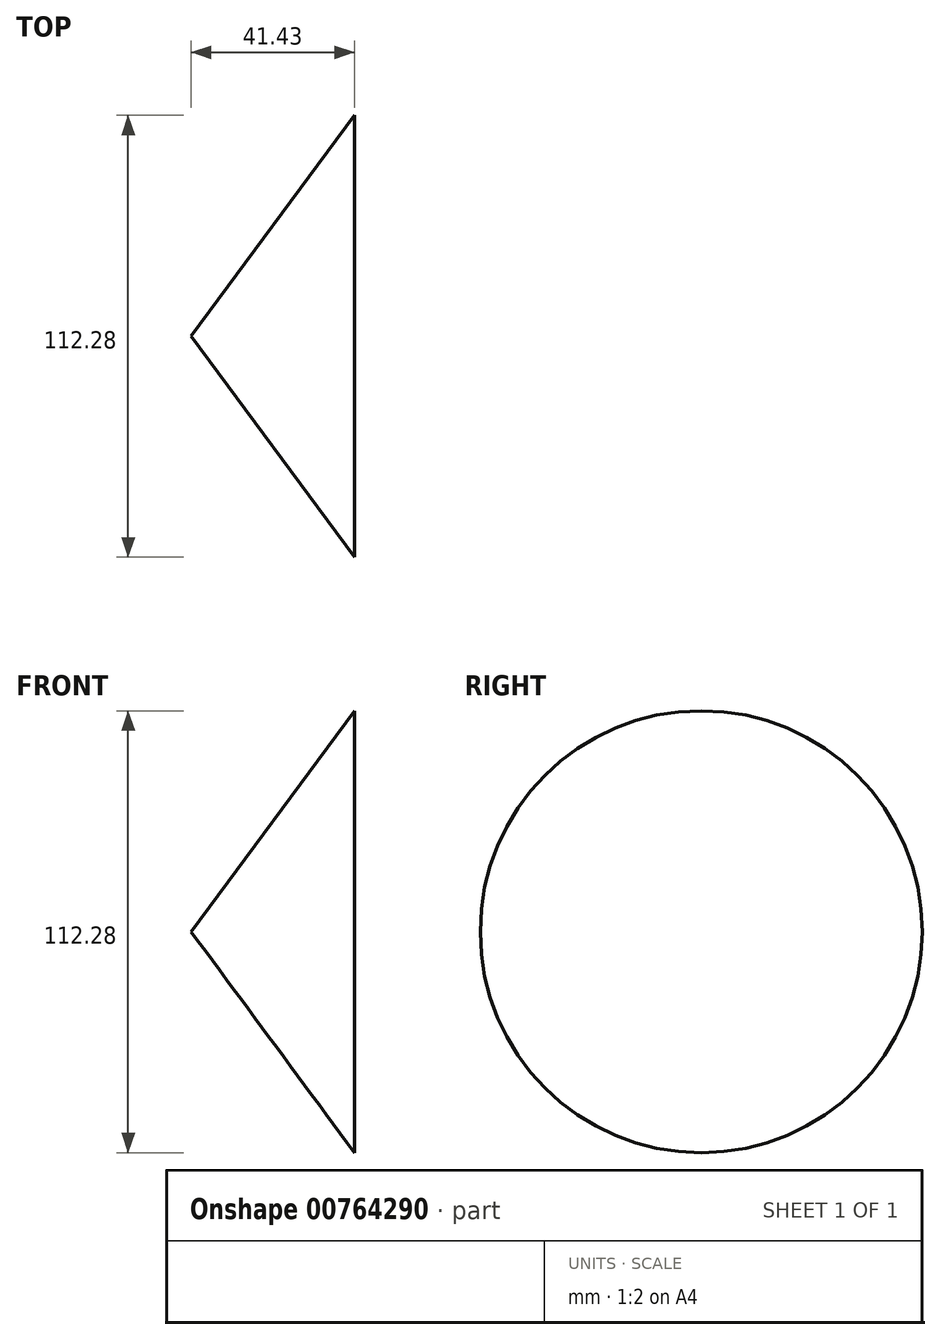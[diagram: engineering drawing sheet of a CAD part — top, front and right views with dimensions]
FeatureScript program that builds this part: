
annotation { "Feature Type Name" : "Feature", "Feature Type Description" : "" }
export const myFeature = defineFeature(function(context is Context, id is Id, definition is map)
    precondition{}
    {
        {
            var Q0;
            Q0=qCreatedBy(makeId("Front.planeOp"),FACE);
            var sketch = newSketch(context, id + "F0", { "sketchPlane" : qUnion([Q0])});
            skLineSegment(sketch, "E0", {"start": v(0, 56.14) * mm, "end": v(-41.43, 0) * mm});
            skLineSegment(sketch, "E1", {"start": v(-41.43, 0) * mm, "end": v(0, 0) * mm});
            skLineSegment(sketch, "E2", {"start": v(0, 0) * mm, "end": v(0, 56.14) * mm});
            skSolve(sketch);
        }
        {
            var Q0;
            Q0 = qSketchRegion(id + "F0", true);
            var Q1;
            Q1=sQuery(id+"F0.wireOp",EDGE,"E1");
            revolve(context, id + "F1", {"surfaceOperationType" : NewSurfaceOperationType.NEW, "entities" : qUnion([Q0]), "axis" : qUnion([Q1]), "revolveType" : RevolveType.FULL});
        }
        {
            var Q0;
            Q0=qCreatedBy(makeId("Right.planeOp"),FACE);
            var sketch = newSketch(context, id + "F2", { "sketchPlane" : qUnion([Q0])});
            skLineSegment(sketch, "E3", {"start": v(-32.9, 76.23) * mm, "end": v(-32.9, -77.7) * mm});
            skSolve(sketch);
        }
        {
            var Q0;
            Q0=sQuery(id+"F2.wireOp",EDGE,"E3");
            extrude(context, id + "F3", {"bodyType" : ToolBodyType.SURFACE, "surfaceEntities" : qUnion([Q0]), "endBound" : BoundingType.SYMMETRIC, "oppositeDirection" : true, "depth" : 114.3 * mm, "offsetDistance" : 25.4 * mm});
        }
        {
            var Q0;
            Q0=qCreatedBy(makeId("Front.planeOp"),FACE);
            var sketch = newSketch(context, id + "F4", { "sketchPlane" : qUnion([Q0])});
            skLineSegment(sketch, "E4", {"start": v(-21.32, -78.3) * mm, "end": v(-21.32, 76.26) * mm});
            skSolve(sketch);
        }
        {
            var Q0;
            Q0 = qSketchRegion(id + "F4", true);
            var Q1;
            Q1=sQuery(id+"F4.wireOp",EDGE,"E4");
            extrude(context, id + "F5", {"entities" : qUnion([Q0]), "bodyType" : ToolBodyType.SURFACE, "surfaceEntities" : qUnion([Q1]), "endBound" : BoundingType.SYMMETRIC, "oppositeDirection" : true, "depth" : 114.8 * mm, "offsetDistance" : 25.4 * mm});
        }
    });
